# Revit family: Palace_Multi_XO_Standard
name_source: partatom
category: Doors
revit_build: Autodesk Revit 2014 (Build: 20130308_1515(x64)
units: mm (PartAtom-declared; Revit-internal decimal feet)

## types (36) — shared parameters
Centered In Wall = Yes
Custom Sash Width Left = 600 mm  [stored 1.9685 ft]
DG Air Gap Thickness = 12 mm  [stored 0.0393701 ft]
DG Thickness Calc = 6 mm  [stored 0.019685 ft]
Description = High performance sliding door, XO
Double Glazing Gasket Material = Double Glazing Gasket Material
Equal Sash Width = Yes
Frame Thickness = 118 mm
Limit Door Height Max = 2390 mm  [stored 7.84121 ft]
Limit Door Height Min = 359 mm  [stored 1.17782 ft]
Limit Door Width Max = 2990 mm  [stored 9.80971 ft]
Limit Door Width Min = 626 mm
Limit Sash Height Max = 2400 mm
Limit Sash Height Min = 300 mm  [stored 0.984252 ft]
Limit Sash Width Max = 1500 mm  [stored 4.92126 ft]
Limit Sash Width Min = 300 mm  [stored 0.984252 ft]
Manufacturer = Crealco
Max System DG One Piece Thickness = 6 mm  [stored 0.019685 ft]
Max System DG Unit Thickness = 25 mm  [stored 0.082021 ft]
Model = Palace
Rough Width = 3 mm  [stored 0.00984252 ft]
Sash Bottom Gap = 31 mm  [stored 0.101706 ft]
Sash Frame Seal = 3 mm  [stored 0.00984252 ft]
Sash Interlocker Width = 40 mm  [stored 0.131234 ft]
Sash Side Gap = 33 mm  [stored 0.108268 ft]
Sash Top Gap = 28 mm  [stored 0.0918635 ft]
Thickness = 758 mm
URL = http://www.crealco.co.za
Wall Closure = By host
zero-valued in all types: Custom Frame Offset From Exterior, Default Sill Height

## per-type parameters (varying)
- Palace-1521XO-1000Pa: Area Left Sash Glazing=1.17 m²; Area Right Sash Glazing=1.17 m²; Custom Door Height=2090 mm  [stored 6.85696 ft]; Custom Door Width=1490 mm  [stored 4.88845 ft]; Custom Windload=1000 mm  [stored 3.28084 ft]; Height=2090 mm  [stored 6.85696 ft]; Interlock Configuration=0 mm  [stored 0 ft]; Intruderprufe Insulated LowE SHGC Value=0.488; Intruderprufe Insulated LowE U Value=3.23; Intruderprufe Insulated SHGC Value=0.539; Intruderprufe Insulated U Value=3.77; Intruderprufe LowE SHGC Value=0.549; Intruderprufe LowE U Value=4.77; Intruderprufe SHGC Value=0.621; Intruderprufe U Value=5.96; Limit Sash Width Left Max=1164 mm  [stored 3.8189 ft]; Limit Sash Width Left Min=300 mm  [stored 0.984252 ft]; Max Pane Area=1.17 m²; Sash Height=2031 mm; Sash Width Left=732 mm  [stored 2.40157 ft]; Sash Width Right=732 mm  [stored 2.40157 ft]; Toughened Safety SHGC Value=0.661; Toughened Safety U Value=6.06; Width=1490 mm  [stored 4.88845 ft]; Windload Design=1000 mm  [stored 3.28084 ft]
- Palace-1521XO-1500Pa: Area Left Sash Glazing=1.17 m²; Area Right Sash Glazing=1.17 m²; Custom Door Height=2090 mm  [stored 6.85696 ft]; Custom Door Width=1490 mm  [stored 4.88845 ft]; Custom Windload=1500 mm  [stored 4.92126 ft]; Height=2090 mm  [stored 6.85696 ft]; Interlock Configuration=1 mm  [stored 0.00328084 ft]; Intruderprufe Insulated LowE SHGC Value=0.488; Intruderprufe Insulated LowE U Value=3.23; Intruderprufe Insulated SHGC Value=0.539; Intruderprufe Insulated U Value=3.77; Intruderprufe LowE SHGC Value=0.549; Intruderprufe LowE U Value=4.77; Intruderprufe SHGC Value=0.621; Intruderprufe U Value=5.96; Limit Sash Width Left Max=1164 mm  [stored 3.8189 ft]; Limit Sash Width Left Min=300 mm  [stored 0.984252 ft]; Max Pane Area=1.17 m²; Sash Height=2031 mm; Sash Width Left=732 mm  [stored 2.40157 ft]; Sash Width Right=732 mm  [stored 2.40157 ft]; Toughened Safety SHGC Value=0.661; Toughened Safety U Value=6.06; Width=1490 mm  [stored 4.88845 ft]; Windload Design=1500 mm  [stored 4.92126 ft]
- Palace-1521XO-2000Pa: Area Left Sash Glazing=1.17 m²; Area Right Sash Glazing=1.17 m²; Custom Door Height=2090 mm  [stored 6.85696 ft]; Custom Door Width=1490 mm  [stored 4.88845 ft]; Custom Windload=2000 mm  [stored 6.56168 ft]; Height=2090 mm  [stored 6.85696 ft]; Interlock Configuration=1 mm  [stored 0.00328084 ft]; Intruderprufe Insulated LowE SHGC Value=0.488; Intruderprufe Insulated LowE U Value=3.23; Intruderprufe Insulated SHGC Value=0.539; Intruderprufe Insulated U Value=3.77; Intruderprufe LowE SHGC Value=0.549; Intruderprufe LowE U Value=4.77; Intruderprufe SHGC Value=0.621; Intruderprufe U Value=5.96; Limit Sash Width Left Max=1164 mm  [stored 3.8189 ft]; Limit Sash Width Left Min=300 mm  [stored 0.984252 ft]; Max Pane Area=1.17 m²; Sash Height=2031 mm; Sash Width Left=732 mm  [stored 2.40157 ft]; Sash Width Right=732 mm  [stored 2.40157 ft]; Toughened Safety SHGC Value=0.661; Toughened Safety U Value=6.06; Width=1490 mm  [stored 4.88845 ft]; Windload Design=2000 mm  [stored 6.56168 ft]
- Palace-1821XO-1000Pa: Area Left Sash Glazing=1.46 m²; Area Right Sash Glazing=1.46 m²; Custom Door Height=2090 mm  [stored 6.85696 ft]; Custom Door Width=1790 mm  [stored 5.8727 ft]; Custom Windload=1000 mm  [stored 3.28084 ft]; Height=2090 mm  [stored 6.85696 ft]; Interlock Configuration=0 mm  [stored 0 ft]; Intruderprufe Insulated LowE SHGC Value=0.498; Intruderprufe Insulated LowE U Value=3.13; Intruderprufe Insulated SHGC Value=0.55; Intruderprufe Insulated U Value=3.7; Intruderprufe LowE SHGC Value=0.561; Intruderprufe LowE U Value=4.68; Intruderprufe SHGC Value=0.634; Intruderprufe U Value=5.94; Limit Sash Width Left Max=1464 mm; Limit Sash Width Left Min=300 mm  [stored 0.984252 ft]; Max Pane Area=1.46 m²; Sash Height=2031 mm; Sash Width Left=882 mm  [stored 2.8937 ft]; Sash Width Right=882 mm  [stored 2.8937 ft]; Toughened Safety SHGC Value=0.676; Toughened Safety U Value=6.07; Width=1790 mm  [stored 5.8727 ft]; Windload Design=1000 mm  [stored 3.28084 ft]
- Palace-1821XO-1500Pa: Area Left Sash Glazing=1.46 m²; Area Right Sash Glazing=1.46 m²; Custom Door Height=2090 mm  [stored 6.85696 ft]; Custom Door Width=1790 mm  [stored 5.8727 ft]; Custom Windload=1500 mm  [stored 4.92126 ft]; Height=2090 mm  [stored 6.85696 ft]; Interlock Configuration=1 mm  [stored 0.00328084 ft]; Intruderprufe Insulated LowE SHGC Value=0.498; Intruderprufe Insulated LowE U Value=3.13; Intruderprufe Insulated SHGC Value=0.55; Intruderprufe Insulated U Value=3.7; Intruderprufe LowE SHGC Value=0.561; Intruderprufe LowE U Value=4.68; Intruderprufe SHGC Value=0.634; Intruderprufe U Value=5.94; Limit Sash Width Left Max=1464 mm; Limit Sash Width Left Min=300 mm  [stored 0.984252 ft]; Max Pane Area=1.46 m²; Sash Height=2031 mm; Sash Width Left=882 mm  [stored 2.8937 ft]; Sash Width Right=882 mm  [stored 2.8937 ft]; Toughened Safety SHGC Value=0.676; Toughened Safety U Value=6.07; Width=1790 mm  [stored 5.8727 ft]; Windload Design=1500 mm  [stored 4.92126 ft]
- Palace-1821XO-2000Pa: Area Left Sash Glazing=1.46 m²; Area Right Sash Glazing=1.46 m²; Custom Door Height=2090 mm  [stored 6.85696 ft]; Custom Door Width=1790 mm  [stored 5.8727 ft]; Custom Windload=2000 mm  [stored 6.56168 ft]; Height=2090 mm  [stored 6.85696 ft]; Interlock Configuration=1 mm  [stored 0.00328084 ft]; Intruderprufe Insulated LowE SHGC Value=0.498; Intruderprufe Insulated LowE U Value=3.13; Intruderprufe Insulated SHGC Value=0.55; Intruderprufe Insulated U Value=3.7; Intruderprufe LowE SHGC Value=0.561; Intruderprufe LowE U Value=4.68; Intruderprufe SHGC Value=0.634; Intruderprufe U Value=5.94; Limit Sash Width Left Max=1464 mm; Limit Sash Width Left Min=300 mm  [stored 0.984252 ft]; Max Pane Area=1.46 m²; Sash Height=2031 mm; Sash Width Left=882 mm  [stored 2.8937 ft]; Sash Width Right=882 mm  [stored 2.8937 ft]; Toughened Safety SHGC Value=0.676; Toughened Safety U Value=6.07; Width=1790 mm  [stored 5.8727 ft]; Windload Design=2000 mm  [stored 6.56168 ft]
- Palace-2121XO-1000Pa: Area Left Sash Glazing=1.74 m²; Area Right Sash Glazing=1.74 m²; Custom Door Height=2090 mm  [stored 6.85696 ft]; Custom Door Width=2090 mm  [stored 6.85696 ft]; Custom Windload=1000 mm  [stored 3.28084 ft]; Height=2090 mm  [stored 6.85696 ft]; Interlock Configuration=1 mm  [stored 0.00328084 ft]; Intruderprufe Insulated LowE SHGC Value=0.505; Intruderprufe Insulated LowE U Value=3.06; Intruderprufe Insulated SHGC Value=0.559; Intruderprufe Insulated U Value=3.64; Intruderprufe LowE SHGC Value=0.569; Intruderprufe LowE U Value=4.62; Intruderprufe SHGC Value=0.644; Intruderprufe U Value=5.96; Limit Sash Width Left Max=1500 mm  [stored 4.92126 ft]; Limit Sash Width Left Min=564 mm  [stored 1.85039 ft]; Max Pane Area=1.74 m²; Sash Height=2031 mm; Sash Width Left=1032 mm  [stored 3.38583 ft]; Sash Width Right=1032 mm  [stored 3.38583 ft]; Toughened Safety SHGC Value=0.686; Toughened Safety U Value=6.07; Width=2090 mm  [stored 6.85696 ft]; Windload Design=1000 mm  [stored 3.28084 ft]
- Palace-2121XO-1500Pa: Area Left Sash Glazing=1.74 m²; Area Right Sash Glazing=1.74 m²; Custom Door Height=2090 mm  [stored 6.85696 ft]; Custom Door Width=2090 mm  [stored 6.85696 ft]; Custom Windload=1500 mm  [stored 4.92126 ft]; Height=2090 mm  [stored 6.85696 ft]; Interlock Configuration=1 mm  [stored 0.00328084 ft]; Intruderprufe Insulated LowE SHGC Value=0.505; Intruderprufe Insulated LowE U Value=3.06; Intruderprufe Insulated SHGC Value=0.559; Intruderprufe Insulated U Value=3.64; Intruderprufe LowE SHGC Value=0.569; Intruderprufe LowE U Value=4.62; Intruderprufe SHGC Value=0.644; Intruderprufe U Value=5.96; Limit Sash Width Left Max=1500 mm  [stored 4.92126 ft]; Limit Sash Width Left Min=564 mm  [stored 1.85039 ft]; Max Pane Area=1.74 m²; Sash Height=2031 mm; Sash Width Left=1032 mm  [stored 3.38583 ft]; Sash Width Right=1032 mm  [stored 3.38583 ft]; Toughened Safety SHGC Value=0.686; Toughened Safety U Value=6.07; Width=2090 mm  [stored 6.85696 ft]; Windload Design=1500 mm  [stored 4.92126 ft]
- Palace-2121XO-2000Pa: Area Left Sash Glazing=1.74 m²; Area Right Sash Glazing=1.74 m²; Custom Door Height=2090 mm  [stored 6.85696 ft]; Custom Door Width=2090 mm  [stored 6.85696 ft]; Custom Windload=2000 mm  [stored 6.56168 ft]; Height=2090 mm  [stored 6.85696 ft]; Interlock Configuration=1 mm  [stored 0.00328084 ft]; Intruderprufe Insulated LowE SHGC Value=0.505; Intruderprufe Insulated LowE U Value=3.06; Intruderprufe Insulated SHGC Value=0.559; Intruderprufe Insulated U Value=3.64; Intruderprufe LowE SHGC Value=0.569; Intruderprufe LowE U Value=4.62; Intruderprufe SHGC Value=0.644; Intruderprufe U Value=5.96; Limit Sash Width Left Max=1500 mm  [stored 4.92126 ft]; Limit Sash Width Left Min=564 mm  [stored 1.85039 ft]; Max Pane Area=1.74 m²; Sash Height=2031 mm; Sash Width Left=1032 mm  [stored 3.38583 ft]; Sash Width Right=1032 mm  [stored 3.38583 ft]; Toughened Safety SHGC Value=0.686; Toughened Safety U Value=6.07; Width=2090 mm  [stored 6.85696 ft]; Windload Design=2000 mm  [stored 6.56168 ft]
- Palace-2421XO-1000Pa: Area Left Sash Glazing=2.02 m²; Area Right Sash Glazing=2.02 m²; Custom Door Height=2090 mm  [stored 6.85696 ft]; Custom Door Width=2390 mm  [stored 7.84121 ft]; Custom Windload=1000 mm  [stored 3.28084 ft]; Height=2090 mm  [stored 6.85696 ft]; Interlock Configuration=1 mm  [stored 0.00328084 ft]; Intruderprufe Insulated LowE SHGC Value=0.51; Intruderprufe Insulated LowE U Value=3; Intruderprufe Insulated SHGC Value=0.565; Intruderprufe Insulated U Value=3.6; Intruderprufe LowE SHGC Value=0.576; Intruderprufe LowE U Value=4.58; Intruderprufe SHGC Value=0.651; Intruderprufe U Value=5.96; Limit Sash Width Left Max=1500 mm  [stored 4.92126 ft]; Limit Sash Width Left Min=864 mm  [stored 2.83465 ft]; Max Pane Area=2.02 m²; Sash Height=2031 mm; Sash Width Left=1182 mm  [stored 3.87795 ft]; Sash Width Right=1182 mm  [stored 3.87795 ft]; Toughened Safety SHGC Value=0.693; Toughened Safety U Value=6.07; Width=2390 mm  [stored 7.84121 ft]; Windload Design=1000 mm  [stored 3.28084 ft]
- Palace-2421XO-1500Pa: Area Left Sash Glazing=2.02 m²; Area Right Sash Glazing=2.02 m²; Custom Door Height=2090 mm  [stored 6.85696 ft]; Custom Door Width=2390 mm  [stored 7.84121 ft]; Custom Windload=1500 mm  [stored 4.92126 ft]; Height=2090 mm  [stored 6.85696 ft]; Interlock Configuration=1 mm  [stored 0.00328084 ft]; Intruderprufe Insulated LowE SHGC Value=0.51; Intruderprufe Insulated LowE U Value=3; Intruderprufe Insulated SHGC Value=0.565; Intruderprufe Insulated U Value=3.6; Intruderprufe LowE SHGC Value=0.576; Intruderprufe LowE U Value=4.58; Intruderprufe SHGC Value=0.651; Intruderprufe U Value=5.96; Limit Sash Width Left Max=1500 mm  [stored 4.92126 ft]; Limit Sash Width Left Min=864 mm  [stored 2.83465 ft]; Max Pane Area=2.02 m²; Sash Height=2031 mm; Sash Width Left=1182 mm  [stored 3.87795 ft]; Sash Width Right=1182 mm  [stored 3.87795 ft]; Toughened Safety SHGC Value=0.693; Toughened Safety U Value=6.07; Width=2390 mm  [stored 7.84121 ft]; Windload Design=1500 mm  [stored 4.92126 ft]
- Palace-2421XO-2000Pa: Area Left Sash Glazing=2.02 m²; Area Right Sash Glazing=2.02 m²; Custom Door Height=2090 mm  [stored 6.85696 ft]; Custom Door Width=2390 mm  [stored 7.84121 ft]; Custom Windload=2000 mm  [stored 6.56168 ft]; Height=2090 mm  [stored 6.85696 ft]; Interlock Configuration=1 mm  [stored 0.00328084 ft]; Intruderprufe Insulated LowE SHGC Value=0.51; Intruderprufe Insulated LowE U Value=3; Intruderprufe Insulated SHGC Value=0.565; Intruderprufe Insulated U Value=3.6; Intruderprufe LowE SHGC Value=0.576; Intruderprufe LowE U Value=4.58; Intruderprufe SHGC Value=0.651; Intruderprufe U Value=5.96; Limit Sash Width Left Max=1500 mm  [stored 4.92126 ft]; Limit Sash Width Left Min=864 mm  [stored 2.83465 ft]; Max Pane Area=2.02 m²; Sash Height=2031 mm; Sash Width Left=1182 mm  [stored 3.87795 ft]; Sash Width Right=1182 mm  [stored 3.87795 ft]; Toughened Safety SHGC Value=0.693; Toughened Safety U Value=6.07; Width=2390 mm  [stored 7.84121 ft]; Windload Design=2000 mm  [stored 6.56168 ft]
- Palace-2721XO-1000Pa: Area Left Sash Glazing=2.3 m²; Area Right Sash Glazing=2.3 m²; Custom Door Height=2090 mm  [stored 6.85696 ft]; Custom Door Width=2690 mm; Custom Windload=1000 mm  [stored 3.28084 ft]; Height=2090 mm  [stored 6.85696 ft]; Interlock Configuration=1 mm  [stored 0.00328084 ft]; Intruderprufe Insulated LowE SHGC Value=0.514; Intruderprufe Insulated LowE U Value=2.96; Intruderprufe Insulated SHGC Value=0.569; Intruderprufe Insulated U Value=3.57; Intruderprufe LowE SHGC Value=0.58; Intruderprufe LowE U Value=4.54; Intruderprufe SHGC Value=0.657; Intruderprufe U Value=5.97; Limit Sash Width Left Max=1500 mm  [stored 4.92126 ft]; Limit Sash Width Left Min=1164 mm  [stored 3.8189 ft]; Max Pane Area=2.3 m²; Sash Height=2031 mm; Sash Width Left=1332 mm  [stored 4.37008 ft]; Sash Width Right=1332 mm  [stored 4.37008 ft]; Toughened Safety SHGC Value=0.699; Toughened Safety U Value=6.07; Width=2690 mm; Windload Design=1000 mm  [stored 3.28084 ft]
- Palace-2721XO-1500Pa: Area Left Sash Glazing=2.3 m²; Area Right Sash Glazing=2.3 m²; Custom Door Height=2090 mm  [stored 6.85696 ft]; Custom Door Width=2690 mm; Custom Windload=1500 mm  [stored 4.92126 ft]; Height=2090 mm  [stored 6.85696 ft]; Interlock Configuration=1 mm  [stored 0.00328084 ft]; Intruderprufe Insulated LowE SHGC Value=0.514; Intruderprufe Insulated LowE U Value=2.96; Intruderprufe Insulated SHGC Value=0.569; Intruderprufe Insulated U Value=3.57; Intruderprufe LowE SHGC Value=0.58; Intruderprufe LowE U Value=4.54; Intruderprufe SHGC Value=0.657; Intruderprufe U Value=5.97; Limit Sash Width Left Max=1500 mm  [stored 4.92126 ft]; Limit Sash Width Left Min=1164 mm  [stored 3.8189 ft]; Max Pane Area=2.3 m²; Sash Height=2031 mm; Sash Width Left=1332 mm  [stored 4.37008 ft]; Sash Width Right=1332 mm  [stored 4.37008 ft]; Toughened Safety SHGC Value=0.699; Toughened Safety U Value=6.07; Width=2690 mm; Windload Design=1500 mm  [stored 4.92126 ft]
- Palace-2721XO-2000Pa: Area Left Sash Glazing=2.3 m²; Area Right Sash Glazing=2.3 m²; Custom Door Height=2090 mm  [stored 6.85696 ft]; Custom Door Width=2690 mm; Custom Windload=2000 mm  [stored 6.56168 ft]; Height=2090 mm  [stored 6.85696 ft]; Interlock Configuration=1 mm  [stored 0.00328084 ft]; Intruderprufe Insulated LowE SHGC Value=0.514; Intruderprufe Insulated LowE U Value=2.96; Intruderprufe Insulated SHGC Value=0.569; Intruderprufe Insulated U Value=3.57; Intruderprufe LowE SHGC Value=0.58; Intruderprufe LowE U Value=4.54; Intruderprufe SHGC Value=0.657; Intruderprufe U Value=5.97; Limit Sash Width Left Max=1500 mm  [stored 4.92126 ft]; Limit Sash Width Left Min=1164 mm  [stored 3.8189 ft]; Max Pane Area=2.3 m²; Sash Height=2031 mm; Sash Width Left=1332 mm  [stored 4.37008 ft]; Sash Width Right=1332 mm  [stored 4.37008 ft]; Toughened Safety SHGC Value=0.699; Toughened Safety U Value=6.07; Width=2690 mm; Windload Design=2000 mm  [stored 6.56168 ft]
- Palace-3021XO-1000Pa: Area Left Sash Glazing=2.59 m²; Area Right Sash Glazing=2.59 m²; Custom Door Height=2090 mm  [stored 6.85696 ft]; Custom Door Width=2990 mm  [stored 9.80971 ft]; Custom Windload=1000 mm  [stored 3.28084 ft]; Height=2090 mm  [stored 6.85696 ft]; Interlock Configuration=1 mm  [stored 0.00328084 ft]; Intruderprufe Insulated LowE SHGC Value=0.518; Intruderprufe Insulated LowE U Value=2.93; Intruderprufe Insulated SHGC Value=0.573; Intruderprufe Insulated U Value=3.54; Intruderprufe LowE SHGC Value=0; Intruderprufe LowE U Value=7.9; Intruderprufe SHGC Value=0; Intruderprufe U Value=7.9; Limit Sash Width Left Max=1500 mm  [stored 4.92126 ft]; Limit Sash Width Left Min=1464 mm; Max Pane Area=2.59 m²; Sash Height=2031 mm; Sash Width Left=1482 mm  [stored 4.8622 ft]; Sash Width Right=1482 mm  [stored 4.8622 ft]; Toughened Safety SHGC Value=0.704; Toughened Safety U Value=6.07; Width=2990 mm  [stored 9.80971 ft]; Windload Design=1000 mm  [stored 3.28084 ft]
- Palace-3021XO-1500Pa: Area Left Sash Glazing=2.59 m²; Area Right Sash Glazing=2.59 m²; Custom Door Height=2090 mm  [stored 6.85696 ft]; Custom Door Width=2990 mm  [stored 9.80971 ft]; Custom Windload=1500 mm  [stored 4.92126 ft]; Height=2090 mm  [stored 6.85696 ft]; Interlock Configuration=1 mm  [stored 0.00328084 ft]; Intruderprufe Insulated LowE SHGC Value=0.518; Intruderprufe Insulated LowE U Value=2.93; Intruderprufe Insulated SHGC Value=0.573; Intruderprufe Insulated U Value=3.54; Intruderprufe LowE SHGC Value=0; Intruderprufe LowE U Value=7.9; Intruderprufe SHGC Value=0; Intruderprufe U Value=7.9; Limit Sash Width Left Max=1500 mm  [stored 4.92126 ft]; Limit Sash Width Left Min=1464 mm; Max Pane Area=2.59 m²; Sash Height=2031 mm; Sash Width Left=1482 mm  [stored 4.8622 ft]; Sash Width Right=1482 mm  [stored 4.8622 ft]; Toughened Safety SHGC Value=0.704; Toughened Safety U Value=6.07; Width=2990 mm  [stored 9.80971 ft]; Windload Design=1500 mm  [stored 4.92126 ft]
- Palace-3021XO-2000Pa: Area Left Sash Glazing=2.59 m²; Area Right Sash Glazing=2.59 m²; Custom Door Height=2090 mm  [stored 6.85696 ft]; Custom Door Width=2990 mm  [stored 9.80971 ft]; Custom Windload=2000 mm  [stored 6.56168 ft]; Height=2090 mm  [stored 6.85696 ft]; Interlock Configuration=1 mm  [stored 0.00328084 ft]; Intruderprufe Insulated LowE SHGC Value=0.518; Intruderprufe Insulated LowE U Value=2.93; Intruderprufe Insulated SHGC Value=0.573; Intruderprufe Insulated U Value=3.54; Intruderprufe LowE SHGC Value=0; Intruderprufe LowE U Value=7.9; Intruderprufe SHGC Value=0; Intruderprufe U Value=7.9; Limit Sash Width Left Max=1500 mm  [stored 4.92126 ft]; Limit Sash Width Left Min=1464 mm; Max Pane Area=2.59 m²; Sash Height=2031 mm; Sash Width Left=1482 mm  [stored 4.8622 ft]; Sash Width Right=1482 mm  [stored 4.8622 ft]; Toughened Safety SHGC Value=0.704; Toughened Safety U Value=6.07; Width=2990 mm  [stored 9.80971 ft]; Windload Design=2000 mm  [stored 6.56168 ft]
- Palace-1524XO-1000Pa: Area Left Sash Glazing=1.36 m²; Area Right Sash Glazing=1.36 m²; Custom Door Height=2390 mm  [stored 7.84121 ft]; Custom Door Width=1490 mm  [stored 4.88845 ft]; Custom Windload=1000 mm  [stored 3.28084 ft]; Height=2390 mm  [stored 7.84121 ft]; Interlock Configuration=1 mm  [stored 0.00328084 ft]; Intruderprufe Insulated LowE SHGC Value=0.496; Intruderprufe Insulated LowE U Value=3.16; Intruderprufe Insulated SHGC Value=0.548; Intruderprufe Insulated U Value=3.71; Intruderprufe LowE SHGC Value=0.559; Intruderprufe LowE U Value=4.71; Intruderprufe SHGC Value=0.632; Intruderprufe U Value=5.94; Limit Sash Width Left Max=1164 mm  [stored 3.8189 ft]; Limit Sash Width Left Min=300 mm  [stored 0.984252 ft]; Max Pane Area=1.36 m²; Sash Height=2331 mm  [stored 7.64764 ft]; Sash Width Left=732 mm  [stored 2.40157 ft]; Sash Width Right=732 mm  [stored 2.40157 ft]; Toughened Safety SHGC Value=0.673; Toughened Safety U Value=6.05; Width=1490 mm  [stored 4.88845 ft]; Windload Design=1000 mm  [stored 3.28084 ft]
- Palace-1524XO-1500Pa: Area Left Sash Glazing=1.36 m²; Area Right Sash Glazing=1.36 m²; Custom Door Height=2390 mm  [stored 7.84121 ft]; Custom Door Width=1490 mm  [stored 4.88845 ft]; Custom Windload=1500 mm  [stored 4.92126 ft]; Height=2390 mm  [stored 7.84121 ft]; Interlock Configuration=1 mm  [stored 0.00328084 ft]; Intruderprufe Insulated LowE SHGC Value=0.496; Intruderprufe Insulated LowE U Value=3.16; Intruderprufe Insulated SHGC Value=0.548; Intruderprufe Insulated U Value=3.71; Intruderprufe LowE SHGC Value=0.559; Intruderprufe LowE U Value=4.71; Intruderprufe SHGC Value=0.632; Intruderprufe U Value=5.94; Limit Sash Width Left Max=1164 mm  [stored 3.8189 ft]; Limit Sash Width Left Min=300 mm  [stored 0.984252 ft]; Max Pane Area=1.36 m²; Sash Height=2331 mm  [stored 7.64764 ft]; Sash Width Left=732 mm  [stored 2.40157 ft]; Sash Width Right=732 mm  [stored 2.40157 ft]; Toughened Safety SHGC Value=0.673; Toughened Safety U Value=6.05; Width=1490 mm  [stored 4.88845 ft]; Windload Design=1500 mm  [stored 4.92126 ft]
- Palace-1524XO-2000Pa: Area Left Sash Glazing=1.36 m²; Area Right Sash Glazing=1.36 m²; Custom Door Height=2390 mm  [stored 7.84121 ft]; Custom Door Width=1490 mm  [stored 4.88845 ft]; Custom Windload=2000 mm  [stored 6.56168 ft]; Height=2390 mm  [stored 7.84121 ft]; Interlock Configuration=1 mm  [stored 0.00328084 ft]; Intruderprufe Insulated LowE SHGC Value=0.496; Intruderprufe Insulated LowE U Value=3.16; Intruderprufe Insulated SHGC Value=0.548; Intruderprufe Insulated U Value=3.71; Intruderprufe LowE SHGC Value=0.559; Intruderprufe LowE U Value=4.71; Intruderprufe SHGC Value=0.632; Intruderprufe U Value=5.94; Limit Sash Width Left Max=1164 mm  [stored 3.8189 ft]; Limit Sash Width Left Min=300 mm  [stored 0.984252 ft]; Max Pane Area=1.36 m²; Sash Height=2331 mm  [stored 7.64764 ft]; Sash Width Left=732 mm  [stored 2.40157 ft]; Sash Width Right=732 mm  [stored 2.40157 ft]; Toughened Safety SHGC Value=0.673; Toughened Safety U Value=6.05; Width=1490 mm  [stored 4.88845 ft]; Windload Design=2000 mm  [stored 6.56168 ft]
- Palace-1824XO-1000Pa: Area Left Sash Glazing=1.69 m²; Area Right Sash Glazing=1.69 m²; Custom Door Height=2390 mm  [stored 7.84121 ft]; Custom Door Width=1790 mm  [stored 5.8727 ft]; Custom Windload=1000 mm  [stored 3.28084 ft]; Height=2390 mm  [stored 7.84121 ft]; Interlock Configuration=1 mm  [stored 0.00328084 ft]; Intruderprufe Insulated LowE SHGC Value=0.506; Intruderprufe Insulated LowE U Value=3.06; Intruderprufe Insulated SHGC Value=0.56; Intruderprufe Insulated U Value=3.63; Intruderprufe LowE SHGC Value=0.571; Intruderprufe LowE U Value=4.62; Intruderprufe SHGC Value=0.645; Intruderprufe U Value=5.94; Limit Sash Width Left Max=1464 mm; Limit Sash Width Left Min=300 mm  [stored 0.984252 ft]; Max Pane Area=1.69 m²; Sash Height=2331 mm  [stored 7.64764 ft]; Sash Width Left=882 mm  [stored 2.8937 ft]; Sash Width Right=882 mm  [stored 2.8937 ft]; Toughened Safety SHGC Value=0.687; Toughened Safety U Value=6.05; Width=1790 mm  [stored 5.8727 ft]; Windload Design=1000 mm  [stored 3.28084 ft]
- Palace-1824XO-1500Pa: Area Left Sash Glazing=1.69 m²; Area Right Sash Glazing=1.69 m²; Custom Door Height=2390 mm  [stored 7.84121 ft]; Custom Door Width=1790 mm  [stored 5.8727 ft]; Custom Windload=1500 mm  [stored 4.92126 ft]; Height=2390 mm  [stored 7.84121 ft]; Interlock Configuration=1 mm  [stored 0.00328084 ft]; Intruderprufe Insulated LowE SHGC Value=0.506; Intruderprufe Insulated LowE U Value=3.06; Intruderprufe Insulated SHGC Value=0.56; Intruderprufe Insulated U Value=3.63; Intruderprufe LowE SHGC Value=0.571; Intruderprufe LowE U Value=4.62; Intruderprufe SHGC Value=0.645; Intruderprufe U Value=5.94; Limit Sash Width Left Max=1464 mm; Limit Sash Width Left Min=300 mm  [stored 0.984252 ft]; Max Pane Area=1.69 m²; Sash Height=2331 mm  [stored 7.64764 ft]; Sash Width Left=882 mm  [stored 2.8937 ft]; Sash Width Right=882 mm  [stored 2.8937 ft]; Toughened Safety SHGC Value=0.687; Toughened Safety U Value=6.05; Width=1790 mm  [stored 5.8727 ft]; Windload Design=1500 mm  [stored 4.92126 ft]
- Palace-1824XO-2000Pa: Area Left Sash Glazing=1.69 m²; Area Right Sash Glazing=1.69 m²; Custom Door Height=2390 mm  [stored 7.84121 ft]; Custom Door Width=1790 mm  [stored 5.8727 ft]; Custom Windload=2000 mm  [stored 6.56168 ft]; Height=2390 mm  [stored 7.84121 ft]; Interlock Configuration=1 mm  [stored 0.00328084 ft]; Intruderprufe Insulated LowE SHGC Value=0.506; Intruderprufe Insulated LowE U Value=3.06; Intruderprufe Insulated SHGC Value=0.56; Intruderprufe Insulated U Value=3.63; Intruderprufe LowE SHGC Value=0.571; Intruderprufe LowE U Value=4.62; Intruderprufe SHGC Value=0.645; Intruderprufe U Value=5.94; Limit Sash Width Left Max=1464 mm; Limit Sash Width Left Min=300 mm  [stored 0.984252 ft]; Max Pane Area=1.69 m²; Sash Height=2331 mm  [stored 7.64764 ft]; Sash Width Left=882 mm  [stored 2.8937 ft]; Sash Width Right=882 mm  [stored 2.8937 ft]; Toughened Safety SHGC Value=0.687; Toughened Safety U Value=6.05; Width=1790 mm  [stored 5.8727 ft]; Windload Design=2000 mm  [stored 6.56168 ft]
- Palace-2124XO-1000Pa: Area Left Sash Glazing=2.02 m²; Area Right Sash Glazing=2.02 m²; Custom Door Height=2390 mm  [stored 7.84121 ft]; Custom Door Width=2090 mm  [stored 6.85696 ft]; Custom Windload=1000 mm  [stored 3.28084 ft]; Height=2390 mm  [stored 7.84121 ft]; Interlock Configuration=1 mm  [stored 0.00328084 ft]; Intruderprufe Insulated LowE SHGC Value=0.513; Intruderprufe Insulated LowE U Value=2.98; Intruderprufe Insulated SHGC Value=0.568; Intruderprufe Insulated U Value=3.75; Intruderprufe LowE SHGC Value=0.579; Intruderprufe LowE U Value=4.56; Intruderprufe SHGC Value=0.655; Intruderprufe U Value=5.94; Limit Sash Width Left Max=1500 mm  [stored 4.92126 ft]; Limit Sash Width Left Min=564 mm  [stored 1.85039 ft]; Max Pane Area=2.02 m²; Sash Height=2331 mm  [stored 7.64764 ft]; Sash Width Left=1032 mm  [stored 3.38583 ft]; Sash Width Right=1032 mm  [stored 3.38583 ft]; Toughened Safety SHGC Value=0.698; Toughened Safety U Value=6.05; Width=2090 mm  [stored 6.85696 ft]; Windload Design=1000 mm  [stored 3.28084 ft]
- Palace-2124XO-1500Pa: Area Left Sash Glazing=2.02 m²; Area Right Sash Glazing=2.02 m²; Custom Door Height=2390 mm  [stored 7.84121 ft]; Custom Door Width=2090 mm  [stored 6.85696 ft]; Custom Windload=1500 mm  [stored 4.92126 ft]; Height=2390 mm  [stored 7.84121 ft]; Interlock Configuration=1 mm  [stored 0.00328084 ft]; Intruderprufe Insulated LowE SHGC Value=0.513; Intruderprufe Insulated LowE U Value=2.98; Intruderprufe Insulated SHGC Value=0.568; Intruderprufe Insulated U Value=3.75; Intruderprufe LowE SHGC Value=0.579; Intruderprufe LowE U Value=4.56; Intruderprufe SHGC Value=0.655; Intruderprufe U Value=5.94; Limit Sash Width Left Max=1500 mm  [stored 4.92126 ft]; Limit Sash Width Left Min=564 mm  [stored 1.85039 ft]; Max Pane Area=2.02 m²; Sash Height=2331 mm  [stored 7.64764 ft]; Sash Width Left=1032 mm  [stored 3.38583 ft]; Sash Width Right=1032 mm  [stored 3.38583 ft]; Toughened Safety SHGC Value=0.698; Toughened Safety U Value=6.05; Width=2090 mm  [stored 6.85696 ft]; Windload Design=1500 mm  [stored 4.92126 ft]
- Palace-2124XO-2000Pa: Area Left Sash Glazing=2.02 m²; Area Right Sash Glazing=2.02 m²; Custom Door Height=2390 mm  [stored 7.84121 ft]; Custom Door Width=2090 mm  [stored 6.85696 ft]; Custom Windload=2000 mm  [stored 6.56168 ft]; Height=2390 mm  [stored 7.84121 ft]; Interlock Configuration=1 mm  [stored 0.00328084 ft]; Intruderprufe Insulated LowE SHGC Value=0.513; Intruderprufe Insulated LowE U Value=2.98; Intruderprufe Insulated SHGC Value=0.568; Intruderprufe Insulated U Value=3.75; Intruderprufe LowE SHGC Value=0.579; Intruderprufe LowE U Value=4.56; Intruderprufe SHGC Value=0.655; Intruderprufe U Value=5.94; Limit Sash Width Left Max=1500 mm  [stored 4.92126 ft]; Limit Sash Width Left Min=564 mm  [stored 1.85039 ft]; Max Pane Area=2.02 m²; Sash Height=2331 mm  [stored 7.64764 ft]; Sash Width Left=1032 mm  [stored 3.38583 ft]; Sash Width Right=1032 mm  [stored 3.38583 ft]; Toughened Safety SHGC Value=0.698; Toughened Safety U Value=6.05; Width=2090 mm  [stored 6.85696 ft]; Windload Design=2000 mm  [stored 6.56168 ft]
- Palace-2424XO-1000Pa: Area Left Sash Glazing=2.34 m²; Area Right Sash Glazing=2.34 m²; Custom Door Height=2390 mm  [stored 7.84121 ft]; Custom Door Width=2390 mm  [stored 7.84121 ft]; Custom Windload=1000 mm  [stored 3.28084 ft]; Height=2390 mm  [stored 7.84121 ft]; Interlock Configuration=1 mm  [stored 0.00328084 ft]; Intruderprufe Insulated LowE SHGC Value=0.519; Intruderprufe Insulated LowE U Value=2.93; Intruderprufe Insulated SHGC Value=0.574; Intruderprufe Insulated U Value=3.53; Intruderprufe LowE SHGC Value=0.585; Intruderprufe LowE U Value=4.51; Intruderprufe SHGC Value=0.663; Intruderprufe U Value=5.94; Limit Sash Width Left Max=1500 mm  [stored 4.92126 ft]; Limit Sash Width Left Min=864 mm  [stored 2.83465 ft]; Max Pane Area=2.34 m²; Sash Height=2331 mm  [stored 7.64764 ft]; Sash Width Left=1182 mm  [stored 3.87795 ft]; Sash Width Right=1182 mm  [stored 3.87795 ft]; Toughened Safety SHGC Value=0.705; Toughened Safety U Value=6.05; Width=2390 mm  [stored 7.84121 ft]; Windload Design=1000 mm  [stored 3.28084 ft]
- Palace-2424XO-1500Pa: Area Left Sash Glazing=2.34 m²; Area Right Sash Glazing=2.34 m²; Custom Door Height=2390 mm  [stored 7.84121 ft]; Custom Door Width=2390 mm  [stored 7.84121 ft]; Custom Windload=1500 mm  [stored 4.92126 ft]; Height=2390 mm  [stored 7.84121 ft]; Interlock Configuration=1 mm  [stored 0.00328084 ft]; Intruderprufe Insulated LowE SHGC Value=0.519; Intruderprufe Insulated LowE U Value=2.93; Intruderprufe Insulated SHGC Value=0.574; Intruderprufe Insulated U Value=3.53; Intruderprufe LowE SHGC Value=0.585; Intruderprufe LowE U Value=4.51; Intruderprufe SHGC Value=0.663; Intruderprufe U Value=5.94; Limit Sash Width Left Max=1500 mm  [stored 4.92126 ft]; Limit Sash Width Left Min=864 mm  [stored 2.83465 ft]; Max Pane Area=2.34 m²; Sash Height=2331 mm  [stored 7.64764 ft]; Sash Width Left=1182 mm  [stored 3.87795 ft]; Sash Width Right=1182 mm  [stored 3.87795 ft]; Toughened Safety SHGC Value=0.705; Toughened Safety U Value=6.05; Width=2390 mm  [stored 7.84121 ft]; Windload Design=1500 mm  [stored 4.92126 ft]
- Palace-2424XO-2000Pa: Area Left Sash Glazing=2.34 m²; Area Right Sash Glazing=2.34 m²; Custom Door Height=2390 mm  [stored 7.84121 ft]; Custom Door Width=2390 mm  [stored 7.84121 ft]; Custom Windload=2000 mm  [stored 6.56168 ft]; Height=2390 mm  [stored 7.84121 ft]; Interlock Configuration=1 mm  [stored 0.00328084 ft]; Intruderprufe Insulated LowE SHGC Value=0.519; Intruderprufe Insulated LowE U Value=2.93; Intruderprufe Insulated SHGC Value=0.574; Intruderprufe Insulated U Value=3.53; Intruderprufe LowE SHGC Value=0.585; Intruderprufe LowE U Value=4.51; Intruderprufe SHGC Value=0.663; Intruderprufe U Value=5.94; Limit Sash Width Left Max=1500 mm  [stored 4.92126 ft]; Limit Sash Width Left Min=864 mm  [stored 2.83465 ft]; Max Pane Area=2.34 m²; Sash Height=2331 mm  [stored 7.64764 ft]; Sash Width Left=1182 mm  [stored 3.87795 ft]; Sash Width Right=1182 mm  [stored 3.87795 ft]; Toughened Safety SHGC Value=0.705; Toughened Safety U Value=6.05; Width=2390 mm  [stored 7.84121 ft]; Windload Design=2000 mm  [stored 6.56168 ft]
- Palace-2724XO-1000Pa: Area Left Sash Glazing=2.67 m²; Area Right Sash Glazing=2.67 m²; Custom Door Height=2390 mm  [stored 7.84121 ft]; Custom Door Width=2690 mm; Custom Windload=1000 mm  [stored 3.28084 ft]; Height=2390 mm  [stored 7.84121 ft]; Interlock Configuration=1 mm  [stored 0.00328084 ft]; Intruderprufe Insulated LowE SHGC Value=5.23; Intruderprufe Insulated LowE U Value=2.88; Intruderprufe Insulated SHGC Value=0.579; Intruderprufe Insulated U Value=3.5; Intruderprufe LowE SHGC Value=0; Intruderprufe LowE U Value=7.9; Intruderprufe SHGC Value=0; Intruderprufe U Value=7.9; Limit Sash Width Left Max=1500 mm  [stored 4.92126 ft]; Limit Sash Width Left Min=1164 mm  [stored 3.8189 ft]; Max Pane Area=2.67 m²; Sash Height=2331 mm  [stored 7.64764 ft]; Sash Width Left=1332 mm  [stored 4.37008 ft]; Sash Width Right=1332 mm  [stored 4.37008 ft]; Toughened Safety SHGC Value=0.712; Toughened Safety U Value=6.05; Width=2690 mm; Windload Design=1000 mm  [stored 3.28084 ft]
- Palace-2724XO-1500Pa: Area Left Sash Glazing=2.67 m²; Area Right Sash Glazing=2.67 m²; Custom Door Height=2390 mm  [stored 7.84121 ft]; Custom Door Width=2690 mm; Custom Windload=1500 mm  [stored 4.92126 ft]; Height=2390 mm  [stored 7.84121 ft]; Interlock Configuration=1 mm  [stored 0.00328084 ft]; Intruderprufe Insulated LowE SHGC Value=5.23; Intruderprufe Insulated LowE U Value=2.88; Intruderprufe Insulated SHGC Value=0.579; Intruderprufe Insulated U Value=3.5; Intruderprufe LowE SHGC Value=0; Intruderprufe LowE U Value=7.9; Intruderprufe SHGC Value=0; Intruderprufe U Value=7.9; Limit Sash Width Left Max=1500 mm  [stored 4.92126 ft]; Limit Sash Width Left Min=1164 mm  [stored 3.8189 ft]; Max Pane Area=2.67 m²; Sash Height=2331 mm  [stored 7.64764 ft]; Sash Width Left=1332 mm  [stored 4.37008 ft]; Sash Width Right=1332 mm  [stored 4.37008 ft]; Toughened Safety SHGC Value=0.712; Toughened Safety U Value=6.05; Width=2690 mm; Windload Design=1500 mm  [stored 4.92126 ft]
- Palace-2724XO-2000Pa: Area Left Sash Glazing=2.67 m²; Area Right Sash Glazing=2.67 m²; Custom Door Height=2390 mm  [stored 7.84121 ft]; Custom Door Width=2690 mm; Custom Windload=2000 mm  [stored 6.56168 ft]; Height=2390 mm  [stored 7.84121 ft]; Interlock Configuration=1 mm  [stored 0.00328084 ft]; Intruderprufe Insulated LowE SHGC Value=5.23; Intruderprufe Insulated LowE U Value=2.88; Intruderprufe Insulated SHGC Value=0.579; Intruderprufe Insulated U Value=3.5; Intruderprufe LowE SHGC Value=0; Intruderprufe LowE U Value=7.9; Intruderprufe SHGC Value=0; Intruderprufe U Value=7.9; Limit Sash Width Left Max=1500 mm  [stored 4.92126 ft]; Limit Sash Width Left Min=1164 mm  [stored 3.8189 ft]; Max Pane Area=2.67 m²; Sash Height=2331 mm  [stored 7.64764 ft]; Sash Width Left=1332 mm  [stored 4.37008 ft]; Sash Width Right=1332 mm  [stored 4.37008 ft]; Toughened Safety SHGC Value=0.712; Toughened Safety U Value=6.05; Width=2690 mm; Windload Design=2000 mm  [stored 6.56168 ft]
- Palace-3024XO-1000Pa: Area Left Sash Glazing=3 m²; Area Right Sash Glazing=3 m²; Custom Door Height=2390 mm  [stored 7.84121 ft]; Custom Door Width=2990 mm  [stored 9.80971 ft]; Custom Windload=1000 mm  [stored 3.28084 ft]; Height=2390 mm  [stored 7.84121 ft]; Interlock Configuration=1 mm  [stored 0.00328084 ft]; Intruderprufe Insulated LowE SHGC Value=0.526; Intruderprufe Insulated LowE U Value=2.85; Intruderprufe Insulated SHGC Value=0.583; Intruderprufe Insulated U Value=3.47; Intruderprufe LowE SHGC Value=0; Intruderprufe LowE U Value=7.9; Intruderprufe SHGC Value=0; Intruderprufe U Value=7.9; Limit Sash Width Left Max=1500 mm  [stored 4.92126 ft]; Limit Sash Width Left Min=1464 mm; Max Pane Area=3 m²; Sash Height=2331 mm  [stored 7.64764 ft]; Sash Width Left=1482 mm  [stored 4.8622 ft]; Sash Width Right=1482 mm  [stored 4.8622 ft]; Toughened Safety SHGC Value=0.716; Toughened Safety U Value=6.05; Width=2990 mm  [stored 9.80971 ft]; Windload Design=1000 mm  [stored 3.28084 ft]
- Palace-3024XO-1500Pa: Area Left Sash Glazing=3 m²; Area Right Sash Glazing=3 m²; Custom Door Height=2390 mm  [stored 7.84121 ft]; Custom Door Width=2990 mm  [stored 9.80971 ft]; Custom Windload=1500 mm  [stored 4.92126 ft]; Height=2390 mm  [stored 7.84121 ft]; Interlock Configuration=1 mm  [stored 0.00328084 ft]; Intruderprufe Insulated LowE SHGC Value=0.526; Intruderprufe Insulated LowE U Value=2.85; Intruderprufe Insulated SHGC Value=0.583; Intruderprufe Insulated U Value=3.47; Intruderprufe LowE SHGC Value=0; Intruderprufe LowE U Value=7.9; Intruderprufe SHGC Value=0; Intruderprufe U Value=7.9; Limit Sash Width Left Max=1500 mm  [stored 4.92126 ft]; Limit Sash Width Left Min=1464 mm; Max Pane Area=3 m²; Sash Height=2331 mm  [stored 7.64764 ft]; Sash Width Left=1482 mm  [stored 4.8622 ft]; Sash Width Right=1482 mm  [stored 4.8622 ft]; Toughened Safety SHGC Value=0.716; Toughened Safety U Value=6.05; Width=2990 mm  [stored 9.80971 ft]; Windload Design=1500 mm  [stored 4.92126 ft]
- Palace-3024XO-2000Pa: Area Left Sash Glazing=3 m²; Area Right Sash Glazing=3 m²; Custom Door Height=2390 mm  [stored 7.84121 ft]; Custom Door Width=2990 mm  [stored 9.80971 ft]; Custom Windload=2000 mm  [stored 6.56168 ft]; Height=2390 mm  [stored 7.84121 ft]; Interlock Configuration=1 mm  [stored 0.00328084 ft]; Intruderprufe Insulated LowE SHGC Value=0.526; Intruderprufe Insulated LowE U Value=2.85; Intruderprufe Insulated SHGC Value=0.583; Intruderprufe Insulated U Value=3.47; Intruderprufe LowE SHGC Value=0; Intruderprufe LowE U Value=7.9; Intruderprufe SHGC Value=0; Intruderprufe U Value=7.9; Limit Sash Width Left Max=1500 mm  [stored 4.92126 ft]; Limit Sash Width Left Min=1464 mm; Max Pane Area=3 m²; Sash Height=2331 mm  [stored 7.64764 ft]; Sash Width Left=1482 mm  [stored 4.8622 ft]; Sash Width Right=1482 mm  [stored 4.8622 ft]; Toughened Safety SHGC Value=0.716; Toughened Safety U Value=6.05; Width=2990 mm  [stored 9.80971 ft]; Windload Design=2000 mm  [stored 6.56168 ft]

note: [stored X ft] marks values corroborated as IEEE doubles in the binary element streams (Revit-internal decimal feet)

## geometry (parser evidence)
native form markers: Sweep x56
no freeform markers — native parametric forms only
